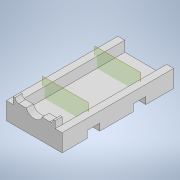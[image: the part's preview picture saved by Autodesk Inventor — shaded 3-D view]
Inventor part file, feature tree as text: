
AUTODESK INVENTOR PART (.ipt)
format: ipt  version: 2020.2 (Build 242310000, 310)  size: 174,080 bytes
history: native  units: mm
features: extrude x6, sketch x6, projected_geometry x3, plane x2
ambient origin geometry x8: Origin, YZ Plane, XZ Plane, XY Plane, X Axis, Y Axis, Z Axis, Center Point
bodies: Solid1 (feature_tree)
feature tree (17):
  extrude  "Extrusion1"  Depth=32.0mm
  extrude  "Extrusion2"  Depth=2.0mm
  extrude  "Extrusion3"  Depth=2.0mm
  extrude  "Extrusion4"  Depth=5.0mm
  plane  "Work Plane1"
  plane  "Work Plane2"
  extrude  "Extrusion5"  Depth=5.0mm
  extrude  "Extrusion6"  Depth=2.0mm
  sketch  "Sketch1"  dims[d0=16.0mm d1=32.0mm]
  sketch  "Sketch2"  dims[d2=2.0mm d3=0.0mm d4=2.0mm]
  sketch  "Sketch3"  dims[d5=2.0mm d6=2.0mm]
  projected_geometry  "Projected Loop1"
  sketch  "Sketch4"  dims[d7=3.0mm d8=0.0mm d9=5.0mm]
  sketch  "Sketch6"  dims[d10=5.0mm d11=9.0mm]
  sketch  "Sketch7"  dims[d12=2.0mm d13=2.0mm d14=2.0mm d15=0.0mm d16=10.0mm d17=0.0mm d18=7.0mm d19=22.0mm d22=2.0mm d23=45.0deg d24=3.6mm d25=0.0mm d26=3.6mm d27=0.0mm]
  projected_geometry  "Projected Loop2"
  projected_geometry  "Projected Loop3"
